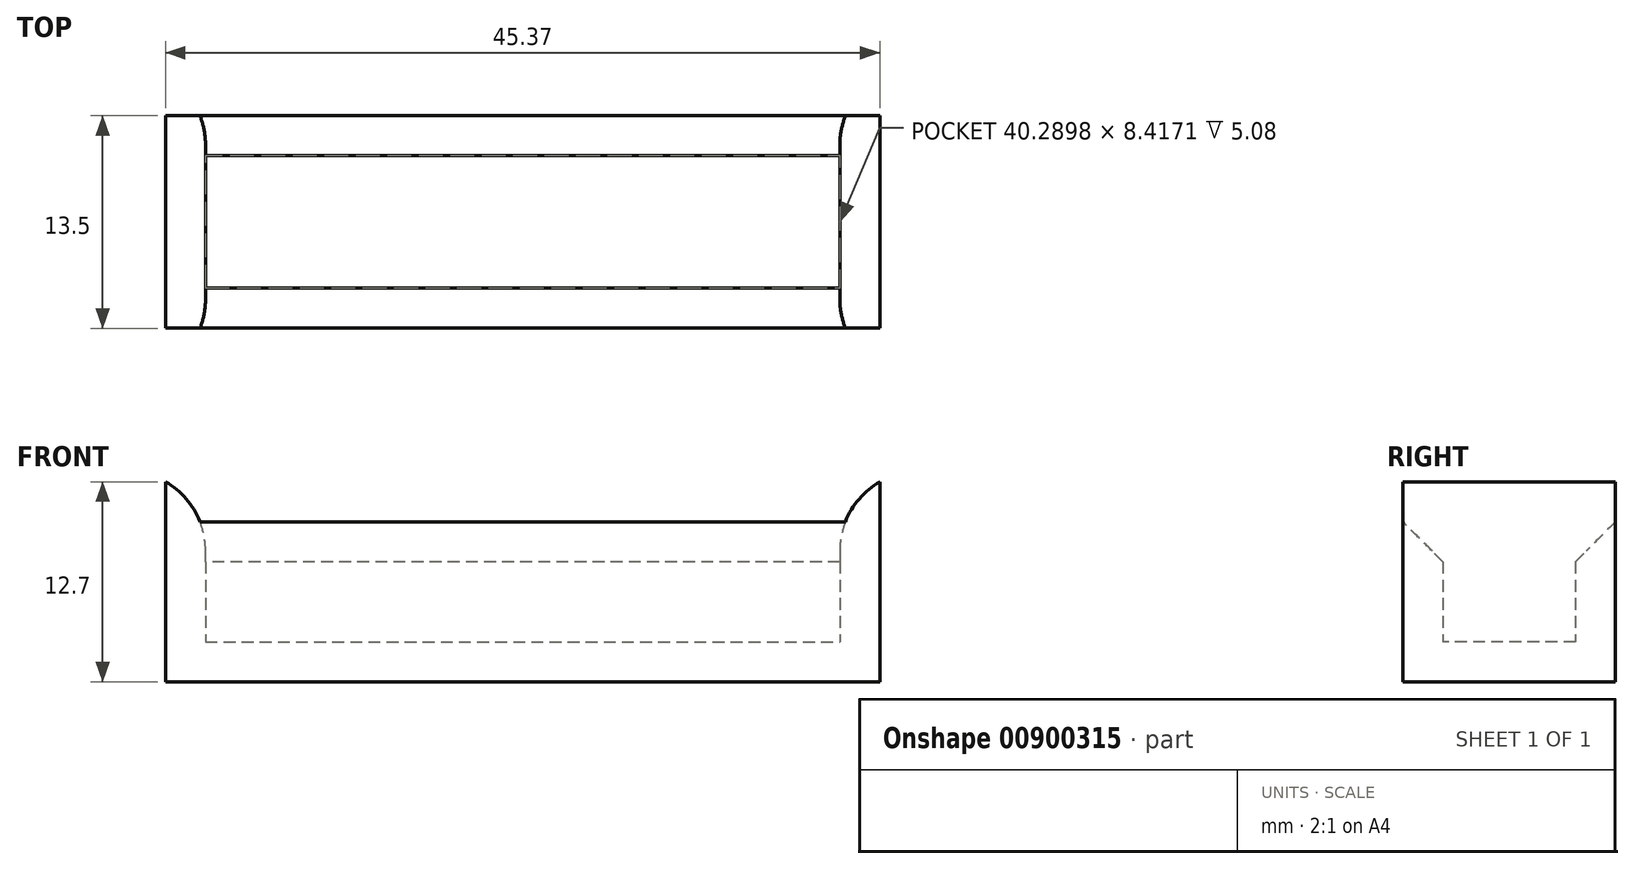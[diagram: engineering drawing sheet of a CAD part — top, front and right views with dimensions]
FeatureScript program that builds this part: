
annotation { "Feature Type Name" : "Feature", "Feature Type Description" : "" }
export const myFeature = defineFeature(function(context is Context, id is Id, definition is map)
    precondition{}
    {
        {
            var Q0;
            Q0=qCreatedBy(makeId("Top.planeOp"),FACE);
            var sketch = newSketch(context, id + "F0", { "sketchPlane" : qUnion([Q0])});
            skLineSegment(sketch, "E0.bottom", {"start": v(0, 0) * mm, "end": v(45.37, 0) * mm});
            skLineSegment(sketch, "E0.top", {"start": v(0, -13.5) * mm, "end": v(45.37, -13.5) * mm});
            skLineSegment(sketch, "E0.left", {"start": v(0, 0) * mm, "end": v(0, -13.5) * mm});
            skLineSegment(sketch, "E0.right", {"start": v(45.37, 0) * mm, "end": v(45.37, -13.5) * mm});
            skSolve(sketch);
        }
        {
            var Q0;
            Q0=makeQuery(id+"F0.imprint","IMPRINT",FACE,{"disambiguationData":[TD([[makeQuery(id+"F0.imprint","IMPRINT",EDGE,{"derivedFrom":sQuery(id+"F0.wireOp",EDGE,"E0.bottom")}),-1.0]])]});
            extrude(context, id + "F1", {"entities" : qUnion([Q0]), "depth" : 12.7 * mm, "offsetDistance" : 25.4 * mm});
        }
        {
            var Q0;
            Q0=makeQuery(id+"F1.opExtrude","CAP_FACE",FACE,{"disambiguationData":[OSD([sQuery(id+"F0.wireOp",EDGE,"E0.bottom"),sQuery(id+"F0.wireOp",EDGE,"E0.top"),sQuery(id+"F0.wireOp",EDGE,"E0.left"),sQuery(id+"F0.wireOp",EDGE,"E0.right")])],"isStart":false});
            shell(context, id + "F2", {"entities" : qUnion([Q0]), "thickness" : 2.54 * mm});
        }
        {
            var Q0;
            {var subQ0=sQuery(id+"F0.wireOp",EDGE,"E0.top");Q0=makeQuery(id+"F2.opShell","OFFSET_EDGE",EDGE,{"disambiguationData":[OSD([subQ0]),TDD([makeQuery(id+"F1.opExtrude","CAP_EDGE",EDGE,{"disambiguationData":[OSD([subQ0])],"isStart":false})])]});}
            var Q1;
            {var subQ0=sQuery(id+"F0.wireOp",EDGE,"E0.bottom");Q1=makeQuery(id+"F2.opShell","OFFSET_EDGE",EDGE,{"disambiguationData":[OSD([subQ0]),TDD([makeQuery(id+"F1.opExtrude","CAP_EDGE",EDGE,{"disambiguationData":[OSD([subQ0])],"isStart":false})])]});}
            chamfer(context, id + "F3", {"entities" : qUnion([Q0, Q1]), "width" : 5.08 * mm, "tangentPropagation" : true});
        }
        {
            var Q0;
            {var subQ0=sQuery(id+"F0.wireOp",EDGE,"E0.right");Q0=makeQuery(id+"F2.opShell","OFFSET_EDGE",EDGE,{"disambiguationData":[OSD([subQ0]),TDD([makeQuery(id+"F1.opExtrude","CAP_EDGE",EDGE,{"disambiguationData":[OSD([subQ0])],"isStart":false})])]});}
            var Q1;
            {var subQ0=sQuery(id+"F0.wireOp",EDGE,"E0.left");Q1=makeQuery(id+"F2.opShell","OFFSET_EDGE",EDGE,{"disambiguationData":[OSD([subQ0]),TDD([makeQuery(id+"F1.opExtrude","CAP_EDGE",EDGE,{"disambiguationData":[OSD([subQ0])],"isStart":false})])]});}
            fillet(context, id + "F4", {"entities" : qUnion([Q0, Q1]), "radius" : 5.08 * mm, "tangentPropagation" : true, "allowEdgeOverflow" : false});
        }
    });
